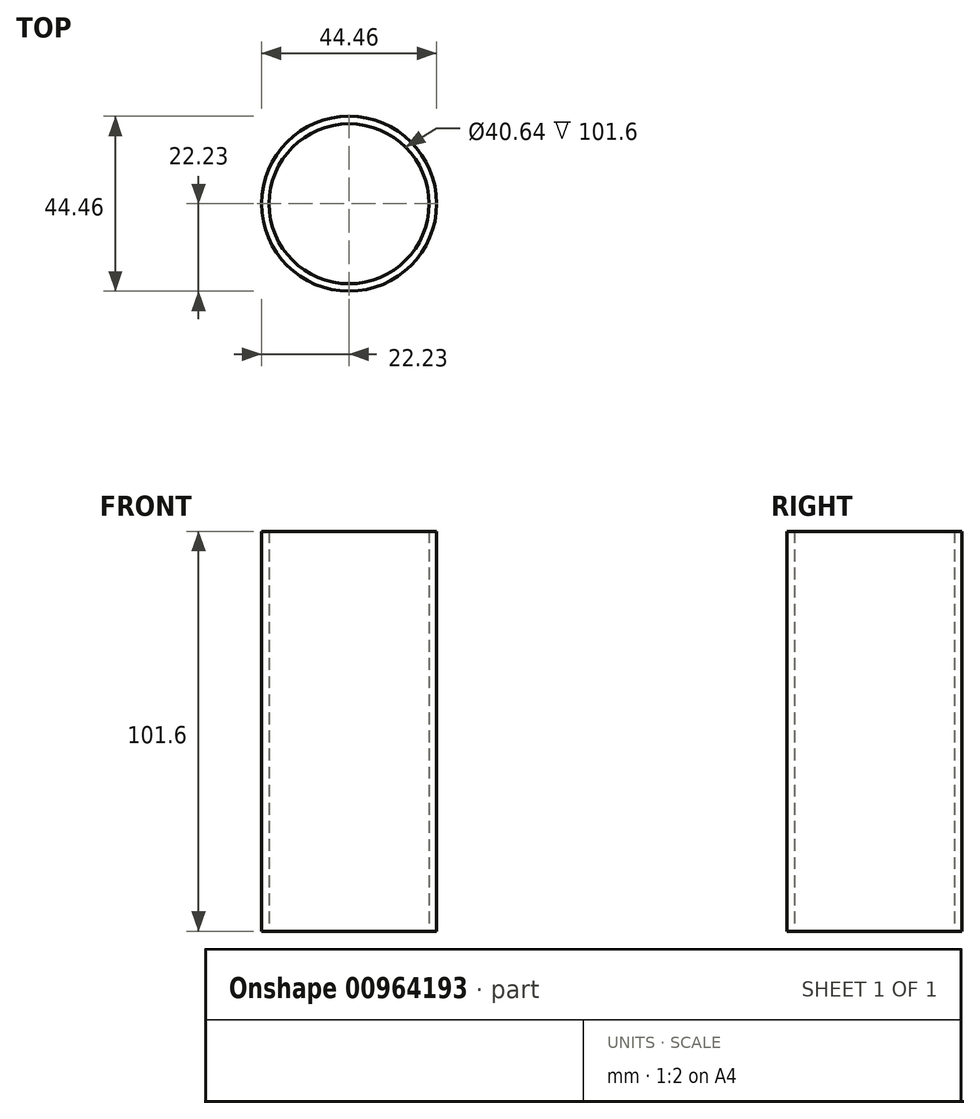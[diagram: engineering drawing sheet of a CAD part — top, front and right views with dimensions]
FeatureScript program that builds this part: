
annotation { "Feature Type Name" : "Feature", "Feature Type Description" : "" }
export const myFeature = defineFeature(function(context is Context, id is Id, definition is map)
    precondition{}
    {
        {
            var Q0;
            Q0=qCreatedBy(makeId("Top.planeOp"),FACE);
            var sketch = newSketch(context, id + "F0", { "sketchPlane" : qUnion([Q0])});
            skCircle(sketch, "E0", {"center": v(0, 0) * mm, "radius": 22.23 * mm});
            skCircle(sketch, "E1", {"center": v(0, 0) * mm, "radius": 20.32 * mm});
            skSolve(sketch);
        }
        {
            var Q0;
            Q0=makeQuery(id+"F0.imprint","IMPRINT",FACE,{"disambiguationData":[TD([[makeQuery(id+"F0.imprint","IMPRINT",EDGE,{"derivedFrom":sQuery(id+"F0.wireOp",EDGE,"E0")}),1.0]])]});
            extrude(context, id + "F1", {"entities" : qUnion([Q0]), "depth" : 101.6 * mm, "offsetDistance" : 25.4 * mm});
        }
    });
